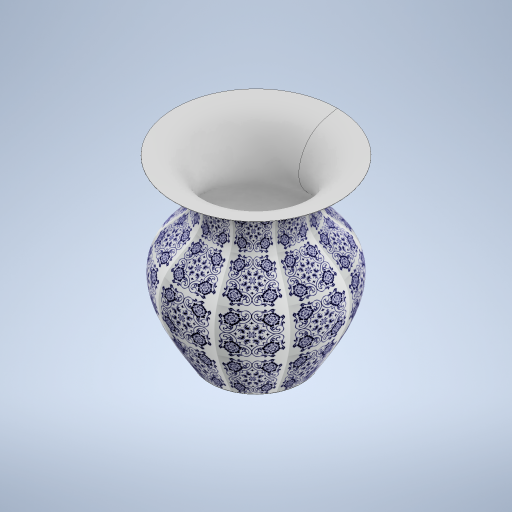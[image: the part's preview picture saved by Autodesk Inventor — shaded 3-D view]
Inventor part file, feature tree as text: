
AUTODESK INVENTOR PART (.ipt)
format: ipt  version: 2024 (Build 280153000, 153)  size: 590,336 bytes
history: native  units: mm
features: revolve x1, shell x1, other x1, sketch x1
ambient origin geometry x8: Origin, YZ Plane, XZ Plane, XY Plane, X Axis, Y Axis, Z Axis, Center Point
bodies: Volumenkörper1 (feature_tree)
feature tree (4):
  revolve  "Umdrehung1"
  shell  "Wandung1"  Thickness=90.0deg
  other  "Volle Abrundung1"
  sketch  "Skizze1"  dims[d1=4.0mm]
